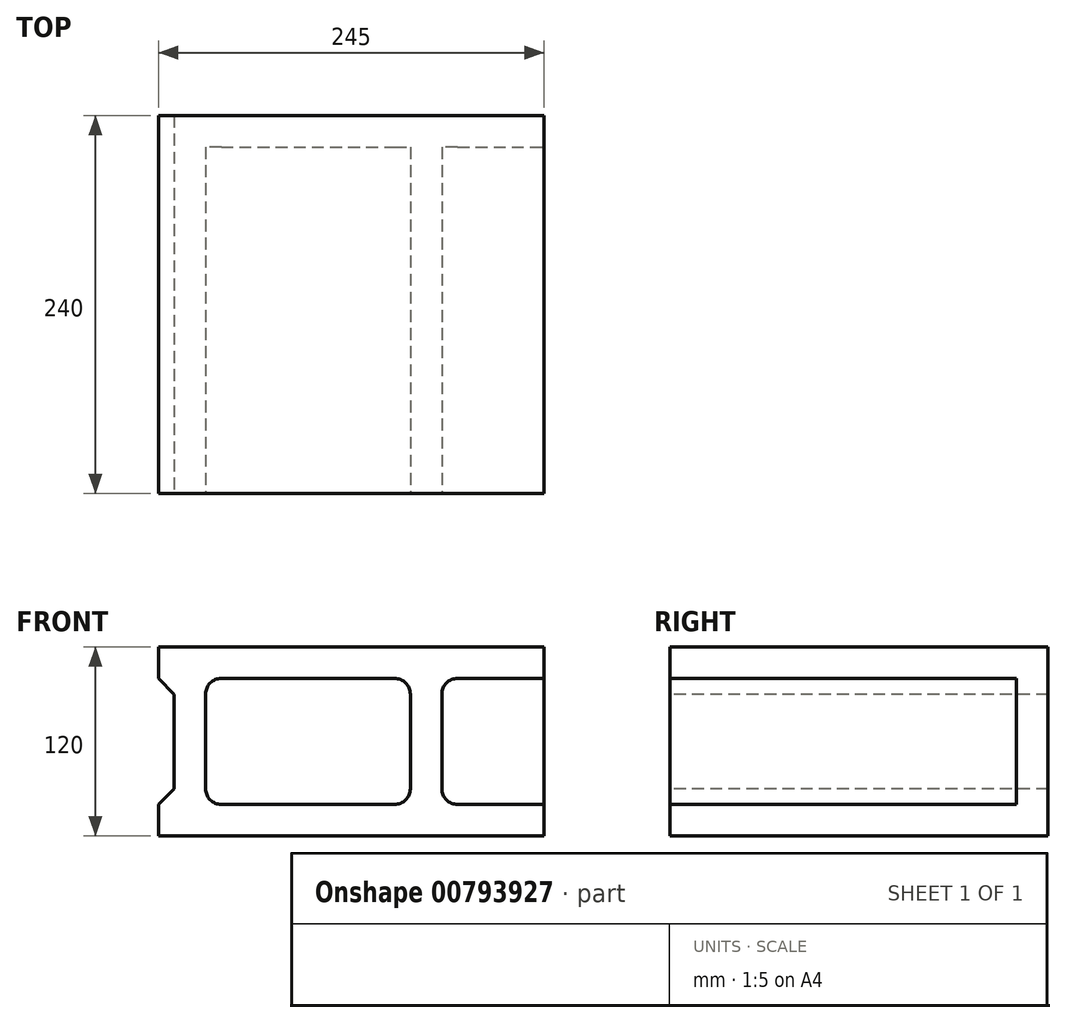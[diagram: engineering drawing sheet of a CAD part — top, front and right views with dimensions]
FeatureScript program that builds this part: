
annotation { "Feature Type Name" : "Feature", "Feature Type Description" : "" }
export const myFeature = defineFeature(function(context is Context, id is Id, definition is map)
    precondition{}
    {
        {
            var Q0;
            Q0=qCreatedBy(makeId("Front.planeOp"),FACE);
            var sketch = newSketch(context, id + "F0", { "sketchPlane" : qUnion([Q0])});
            skLineSegment(sketch, "E0.bottom", {"start": v(-245, -60) * mm, "end": v(0, -60) * mm});
            skLineSegment(sketch, "E0.top", {"start": v(-245, 60) * mm, "end": v(0, 60) * mm});
            skLineSegment(sketch, "E0.left", {"start": v(-245, -60) * mm, "end": v(-245, 60) * mm});
            skPoint(sketch, "E1.oppositeSnap0", {"position": v(-245, 0) * mm});
            skLineSegment(sketch, "E1.bottom", {"start": v(-205, 40) * mm, "end": v(-95, 40) * mm});
            skLineSegment(sketch, "E1.top", {"start": v(-205, -40) * mm, "end": v(-95, -40) * mm});
            skLineSegment(sketch, "E1.left", {"start": v(-215, 30) * mm, "end": v(-215, -30) * mm});
            skLineSegment(sketch, "E1.right", {"start": v(-85, 30) * mm, "end": v(-85, -30) * mm});
            skPoint(sketch, "E2.visualSharp", {"position": v(-85, 40) * mm});
            skArc(sketch, "E2.filletArc", {"start": v(-85, 30) * mm, "mid": v(-87.93, 37.07) * mm, "end": v(-95, 40) * mm});
            skPoint(sketch, "E3.visualSharp", {"position": v(-85, -40) * mm});
            skArc(sketch, "E3.filletArc", {"start": v(-95, -40) * mm, "mid": v(-87.93, -37.07) * mm, "end": v(-85, -30) * mm});
            skArc(sketch, "E4.filletArc", {"start": v(-215, -30) * mm, "mid": v(-212.07, -37.07) * mm, "end": v(-205, -40) * mm});
            skArc(sketch, "E5.filletArc", {"start": v(-205, 40) * mm, "mid": v(-212.07, 37.07) * mm, "end": v(-215, 30) * mm});
            skLineSegment(sketch, "E6.1.0.0", {"start": v(-55, 40) * mm, "end": v(0, 40) * mm});
            skArc(sketch, "E6.1.0.1", {"start": v(-55, 40) * mm, "mid": v(-62.07, 37.07) * mm, "end": v(-65, 30) * mm});
            skLineSegment(sketch, "E6.1.0.2", {"start": v(-65, 30) * mm, "end": v(-65, -30) * mm});
            skArc(sketch, "E6.1.0.3", {"start": v(-65, -30) * mm, "mid": v(-62.07, -37.07) * mm, "end": v(-55, -40) * mm});
            skLineSegment(sketch, "E6.1.0.4", {"start": v(-55, -40) * mm, "end": v(0, -40) * mm});
            skLineSegment(sketch, "E6.direction1", {"start": v(-215, -30) * mm, "end": v(-65, -30) * mm, "construction": true});
            skLineSegment(sketch, "E7", {"start": v(-245, 60) * mm, "end": v(-245, 40) * mm});
            skLineSegment(sketch, "E8", {"start": v(-235, 30) * mm, "end": v(-245, 40) * mm});
            skLineSegment(sketch, "E9", {"start": v(-235, 30) * mm, "end": v(-235, 0) * mm});
            skLineSegment(sketch, "E10", {"start": v(-245, 0) * mm, "end": v(0, 0) * mm, "construction": true});
            skLineSegment(sketch, "E11.MirrorCS", {"start": v(-245, -60) * mm, "end": v(-245, -40) * mm});
            skLineSegment(sketch, "E12.MirrorCS", {"start": v(-235, -30) * mm, "end": v(-235, 0) * mm});
            skLineSegment(sketch, "E13.MirrorCS", {"start": v(-235, -30) * mm, "end": v(-245, -40) * mm});
            skLineSegment(sketch, "E14", {"start": v(0, 60) * mm, "end": v(0, -60) * mm, "construction": true});
            skLineSegment(sketch, "E15", {"start": v(-150, -40) * mm, "end": v(-150, 40) * mm, "construction": true});
            skLineSegment(sketch, "E16", {"start": v(0, 60) * mm, "end": v(0, 40) * mm});
            skLineSegment(sketch, "E17", {"start": v(0, -40) * mm, "end": v(0, -60) * mm});
            skLineSegment(sketch, "E18", {"start": v(0, 40) * mm, "end": v(0, -40) * mm});
            skSolve(sketch);
        }
        {
            var Q0;
            {var subQ4=sQuery(id+"F0.wireOp",EDGE,"E0.bottom");Q0=makeQuery(id+"F0.imprint","IMPRINT",FACE,{"disambiguationData":[TD([[makeQuery(id+"F0.imprint","IMPRINT",EDGE,{"derivedFrom":subQ4}),1.0]])]});}
            var Q1;
            Q1=makeQuery(id+"F0.imprint","IMPRINT",FACE,{"disambiguationData":[TD([[makeQuery(id+"F0.imprint","IMPRINT",EDGE,{"derivedFrom":sQuery(id+"F0.wireOp",EDGE,"E1.bottom")}),-1.0]])]});
            var Q2;
            Q2=makeQuery(id+"F0.imprint","IMPRINT",FACE,{"disambiguationData":[TD([[makeQuery(id+"F0.imprint","IMPRINT",EDGE,{"derivedFrom":sQuery(id+"F0.wireOp",EDGE,"E6.1.0.0")}),-1.0]])]});
            extrude(context, id + "F1", {"entities" : qUnion([Q0, Q1, Q2]), "oppositeDirection" : true, "depth" : 240 * mm, "offsetDistance" : 25 * mm});
        }
        {
            var Q0;
            Q0=makeQuery(id+"F0.imprint","IMPRINT",FACE,{"disambiguationData":[TD([[makeQuery(id+"F0.imprint","IMPRINT",EDGE,{"derivedFrom":sQuery(id+"F0.wireOp",EDGE,"E1.bottom")}),-1.0]])]});
            var Q1;
            Q1=makeQuery(id+"F0.imprint","IMPRINT",FACE,{"disambiguationData":[TD([[makeQuery(id+"F0.imprint","IMPRINT",EDGE,{"derivedFrom":sQuery(id+"F0.wireOp",EDGE,"E6.1.0.0")}),-1.0]])]});
            extrude(context, id + "F2", {"entities" : qUnion([Q0, Q1]), "operationType" : NewBodyOperationType.REMOVE, "oppositeDirection" : true, "depth" : 220 * mm, "offsetDistance" : 25 * mm});
        }
    });
